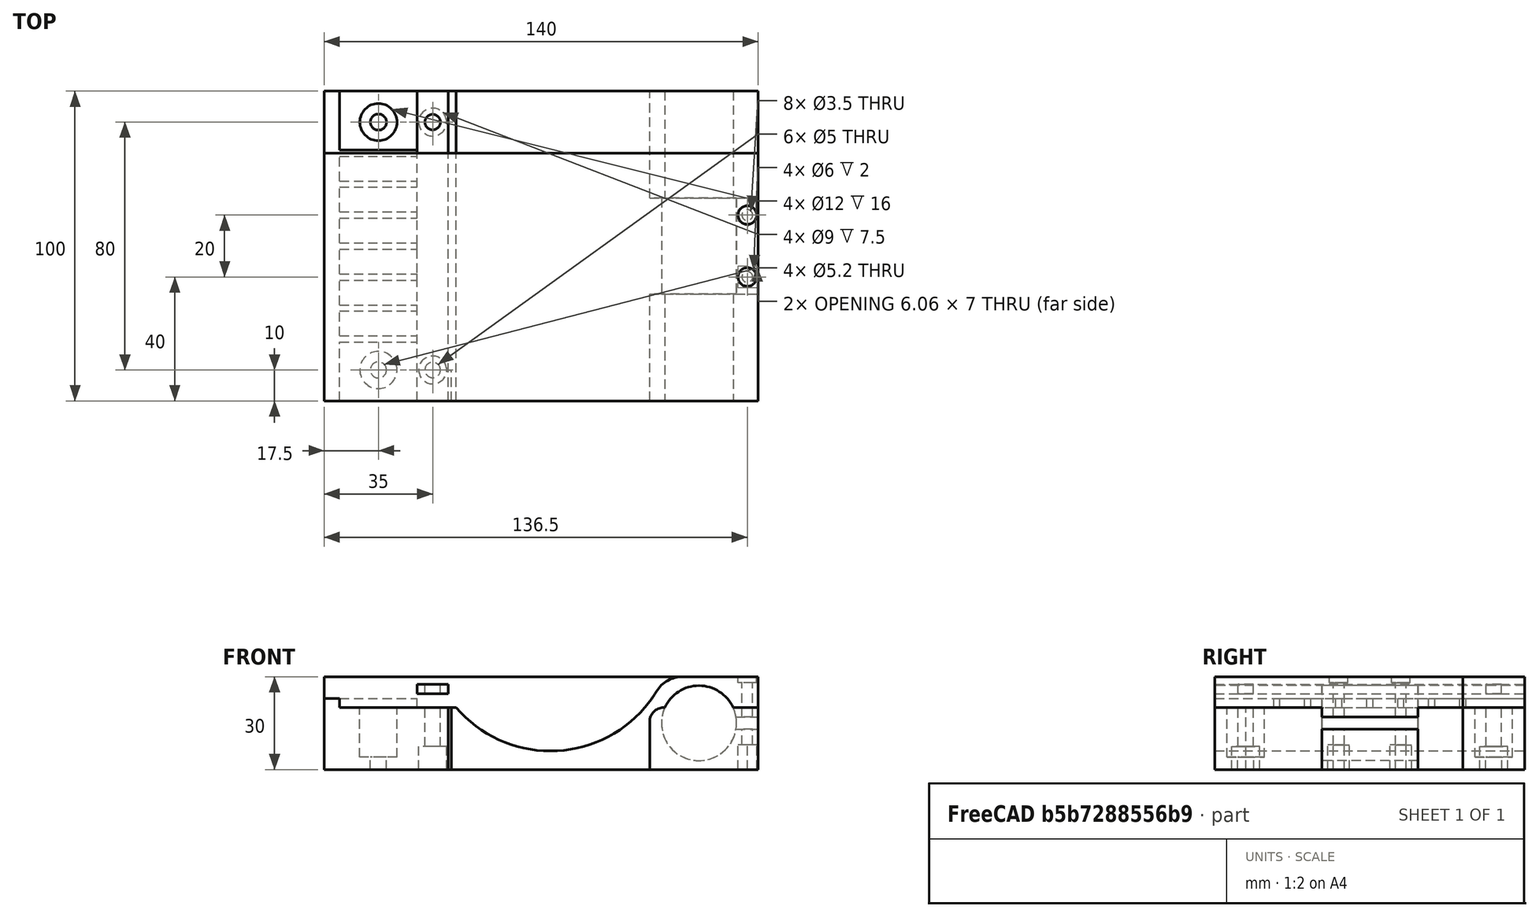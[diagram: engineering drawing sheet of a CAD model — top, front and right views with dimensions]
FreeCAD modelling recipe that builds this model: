
FCSTD DOCUMENT  (FreeCAD 0.18.4R)
Label: vibrator
License: All rights reserved
LicenseURL: http://en.wikipedia.org/wiki/All_rights_reserved
objects: Part::Cylinder×17, Part::Box×16, Part::Cut×10, Part::MultiFuse×5, Part::Fuse×2, Part::RegularPolygon×2, Part::Extrusion×2, PartDesign::Fillet×2, PartDesign::FeatureBase×1, PartDesign::Body×1, Part::Feature×1
note: 59 computed .brp shape members not serialized (recipe doc carries the construction recipe); baked Part::Feature solids carry a one-line shape summary decoded from their .brp

FEATURE [Part::Box] Box  label="Cube"
  AttacherType = Attacher::AttachEngine3D
  Height = 20
  Length = 140
  Width = 100
FEATURE [Part::Cylinder] Cylinder
  Angle = 360
  AttacherType = Attacher::AttachEngine3D
  Height = 20
  Placement = pos=(17.5,10,0) rot=(0,0,1;0rad)
  Radius = 2.6
FEATURE [Part::Cylinder] Cylinder001
  Angle = 360
  AttacherType = Attacher::AttachEngine3D
  Height = 20
  Placement = pos=(17.5,90,0) rot=(0,0,1;0rad)
  Radius = 2.6
FEATURE [Part::Cylinder] Cylinder002
  Angle = 360
  AttacherType = Attacher::AttachEngine3D
  Height = 16
  Placement = pos=(17.5,10,4) rot=(0,0,1;0rad)
  Radius = 6
FEATURE [Part::Cylinder] Cylinder003
  Angle = 360
  AttacherType = Attacher::AttachEngine3D
  Height = 16
  Placement = pos=(17.5,90,4) rot=(0,0,1;0rad)
  Radius = 6
FEATURE [Part::MultiFuse] Fusion
  Shapes = -> [Cylinder,Cylinder002,Cylinder001,Cylinder003]
FEATURE [Part::Cut] Cut
  Base = -> Box
  Tool = -> Fusion
FEATURE [Part::Box] Box001  label="Cube001"
  AttacherType = Attacher::AttachEngine3D
  Height = 3
  Length = 5
  Placement = pos=(0,0,20) rot=(0,0,1;0rad)
  Width = 100
FEATURE [Part::Box] Box002  label="Cube002"
  AttacherType = Attacher::AttachEngine3D
  Height = 3
  Length = 10
  Placement = pos=(30,0,24.5) rot=(0,0,1;0rad)
  Width = 100
FEATURE [Part::Fuse] Fusion001
  Base = -> Cut
  Tool = -> Box001
FEATURE [Part::Box] Box004  label="Cube_far_support"
  AttacherType = Attacher::AttachEngine3D
  Height = 10
  Length = 40
  Placement = pos=(100,0,20) rot=(0,0,1;0rad)
  Width = 100
FEATURE [Part::Box] Box005  label="Cube_delete"
  AttacherType = Attacher::AttachEngine3D
  Height = 30
  Length = 140
  Width = 80
FEATURE [Part::Cylinder] Cylinder004  label="Cylinder_motor"
  Angle = 360
  AttacherType = Attacher::AttachEngine3D
  Height = 31
  Placement = pos=(120.9,65.5,15) rot=(1,0,0;1.5708rad)
  Radius = 12.1
FEATURE [Part::Box] Box006  label="Cube006"
  AttacherType = Attacher::AttachEngine3D
  Height = 3
  Length = 25
  Placement = pos=(5,19,20) rot=(0,0,1;0rad)
  Width = 2
FEATURE [Part::Box] Box007  label="Cube007"
  AttacherType = Attacher::AttachEngine3D
  Height = 3
  Length = 25
  Placement = pos=(5,29,20) rot=(0,0,1;0rad)
  Width = 2
FEATURE [Part::Box] Box008  label="Cube008"
  AttacherType = Attacher::AttachEngine3D
  Height = 3
  Length = 25
  Placement = pos=(5,39,20) rot=(0,0,1;0rad)
  Width = 2
FEATURE [Part::Box] Box009  label="Cube009"
  AttacherType = Attacher::AttachEngine3D
  Height = 3
  Length = 25
  Placement = pos=(5,49,20) rot=(0,0,1;0rad)
  Width = 2
FEATURE [Part::Box] Box010  label="Cube010"
  AttacherType = Attacher::AttachEngine3D
  Height = 3
  Length = 25
  Placement = pos=(5,59,20) rot=(0,0,1;0rad)
  Width = 2
FEATURE [Part::Box] Box011  label="Cube011"
  AttacherType = Attacher::AttachEngine3D
  Height = 3
  Length = 25
  Placement = pos=(5,69,20) rot=(0,0,1;0rad)
  Width = 2
FEATURE [Part::Box] Box012  label="Cube012"
  AttacherType = Attacher::AttachEngine3D
  Height = 3
  Length = 25
  Placement = pos=(5,79,20) rot=(0,0,1;0rad)
  Width = 2
FEATURE [Part::MultiFuse] Fusion004  label="Fusion_tracks"
  Shapes = -> [Box006,Box009,Box008,Box007,Box011,Box010,Box012]
FEATURE [Part::Cylinder] Cylinder005
  Angle = 360
  AttacherType = Attacher::AttachEngine3D
  Height = 20
  Placement = pos=(35,90,0) rot=(0,0,1;0rad)
  Radius = 2.5
FEATURE [Part::Cylinder] Cylinder006
  Angle = 360
  AttacherType = Attacher::AttachEngine3D
  Height = 20
  Placement = pos=(35,10,0) rot=(0,0,1;0rad)
  Radius = 2.5
FEATURE [Part::Cylinder] Cylinder007
  Angle = 360
  AttacherType = Attacher::AttachEngine3D
  Height = 7.5
  Placement = pos=(35,90,0) rot=(0,0,1;0rad)
  Radius = 4.5
FEATURE [Part::Cylinder] Cylinder008
  Angle = 360
  AttacherType = Attacher::AttachEngine3D
  Height = 7.5
  Placement = pos=(35,10,0) rot=(0,0,1;0rad)
  Radius = 4.5
FEATURE [Part::MultiFuse] Fusion005  label="Fusion_1st_support_screw_hole"
  Shapes = -> [Cylinder005,Cylinder008,Cylinder006,Cylinder007]
FEATURE [Part::Cut] Cut002
  Base = -> Fusion001
  Tool = -> Fusion005
FEATURE [Part::Cylinder] Cylinder009
  Angle = 360
  AttacherType = Attacher::AttachEngine3D
  Height = 3
  Placement = pos=(35,10,24.5) rot=(0,0,1;0rad)
  Radius = 2.5
FEATURE [Part::Cylinder] Cylinder010
  Angle = 360
  AttacherType = Attacher::AttachEngine3D
  Height = 3
  Placement = pos=(35,90,24.5) rot=(0,0,1;0rad)
  Radius = 2.5
FEATURE [Part::Cut] Cut003
  Base = -> Box002
  Tool = -> Cylinder009
FEATURE [Part::Cut] Cut004  label="Cut_1st_support_bar"
  Base = -> Cut003
  Tool = -> Cylinder010
FEATURE [Part::Box] Box013  label="Cube013"
  AttacherType = Attacher::AttachEngine3D
  Height = 20
  Length = 35
  Placement = pos=(105,0,0) rot=(0,0,1;0rad)
  Width = 34.5
FEATURE [Part::Box] Box014  label="Cube014"
  AttacherType = Attacher::AttachEngine3D
  Height = 20
  Length = 35
  Placement = pos=(105,65.5,0) rot=(0,0,1;0rad)
  Width = 34.5
FEATURE [Part::Cut] Cut005
  Base = -> Cut002
  Tool = -> Box013
FEATURE [Part::Cut] Cut006
  Base = -> Cut005
  Tool = -> Box014
FEATURE [Part::Cylinder] Cylinder011  label="Cylinder_motor_remove"
  Angle = 360
  AttacherType = Attacher::AttachEngine3D
  Height = 100
  Placement = pos=(120.9,100,15) rot=(1,0,0;1.5708rad)
  Radius = 12.1
FEATURE [Part::Fuse] Fusion006
  Base = -> Cut006
  Tool = -> Box004
FEATURE [Part::Cut] Cut007
  Base = -> Fusion006
  Tool = -> Cylinder011
FEATURE [Part::Cylinder] Cylinder012  label="Cylinder_hole_serrage_01"
  Angle = 360
  AttacherType = Attacher::AttachEngine3D
  Height = 30
  Placement = pos=(136.5,40,0) rot=(0,0,1;0rad)
  Radius = 1.75
FEATURE [Part::Cylinder] Cylinder013  label="Cylinder_hole_serrage_02"
  Angle = 360
  AttacherType = Attacher::AttachEngine3D
  Height = 30
  Placement = pos=(136.5,60,0) rot=(0,0,1;0rad)
  Radius = 1.75
FEATURE [Part::Cylinder] Cylinder014  label="Cylinder_hole_serrage_003"
  Angle = 360
  AttacherType = Attacher::AttachEngine3D
  Height = 2
  Placement = pos=(136.5,40,28) rot=(0,0,1;0rad)
  Radius = 3
FEATURE [Part::Cylinder] Cylinder015  label="Cylinder_hole_serrage_004"
  Angle = 360
  AttacherType = Attacher::AttachEngine3D
  Height = 2
  Placement = pos=(136.5,60,28) rot=(0,0,1;0rad)
  Radius = 3
FEATURE [Part::RegularPolygon] RegularPolygon  label="Regular polygon"
  AttacherType = Attacher::AttachEngine3D
  Circumradius = 3.5
  Polygon = 6
FEATURE [Part::Extrusion] Extrude
  Base = -> RegularPolygon
  Dir = (0,0,1)
  DirMode = 2
  FaceMakerClass = Part::FaceMakerBullseye
  LengthFwd = 8
  LengthRev = 0
  Placement = pos=(136.5,40,0) rot=(0,0,1;0.523599rad)
  Solid = true
  Symmetric = false
FEATURE [Part::RegularPolygon] RegularPolygon001  label="Regular polygon001"
  AttacherType = Attacher::AttachEngine3D
  Circumradius = 3.5
  Polygon = 6
FEATURE [Part::Extrusion] Extrude001
  Base = -> RegularPolygon001
  Dir = (0,0,1)
  DirMode = 2
  FaceMakerClass = Part::FaceMakerBullseye
  LengthFwd = 8
  LengthRev = 0
  Placement = pos=(136.5,60,0) rot=(0,0,1;0.523599rad)
  Solid = true
  Symmetric = false
FEATURE [Part::MultiFuse] Fusion007  label="Fusion_hole_serrage"
  Shapes = -> [Extrude,Cylinder012,Cylinder013,Cylinder015,Cylinder014,Extrude001]
FEATURE [Part::Cut] Cut008
  Base = -> Cut007
  Tool = -> Fusion007
FEATURE [Part::Box] Box015  label="Cube_entrefer"
  AttacherType = Attacher::AttachEngine3D
  Height = 4
  Length = 10
  Placement = pos=(130,0,13) rot=(0,0,1;0rad)
  Width = 100
FEATURE [Part::Cut] Cut009
  Base = -> Cut008
  Tool = -> Box015
FEATURE [Part::Box] Box016  label="Cube015"
  AttacherType = Attacher::AttachEngine3D
  Height = 20
  Length = 1
  Placement = pos=(40,0,0) rot=(0,0,1;0rad)
  Width = 10
FEATURE [Part::Cylinder] Cylinder016  label="Cylinder011"
  Angle = 360
  AttacherType = Attacher::AttachEngine3D
  Height = 100
  Placement = pos=(73,1.02e-14,46) rot=(1,0,0;-1.5708rad)
  Radius = 40
FEATURE [Part::Cut] Cut010
  Base = -> Cut009
  Tool = -> Cylinder016
FEATURE [Part::MultiFuse] Fusion008
  Shapes = -> [Fusion004,Cut010]
FEATURE [PartDesign::FeatureBase] BaseFeature
  BaseFeature = -> Fusion008
FEATURE [PartDesign::Fillet] Fillet
  Base = -> BaseFeature [Edge34]
  BaseFeature = -> BaseFeature
  Radius = 10
FEATURE [PartDesign::Fillet] Fillet001
  Base = -> Fillet [Edge42,Edge129]
  BaseFeature = -> Fillet
  Radius = 4.5
FEATURE [PartDesign::Body] Body
  BaseFeature = -> Fusion008
  Group = -> [BaseFeature,Fillet,Fillet001]
  Origin = -> Origin
  Tip = -> Fillet001
FEATURE [Part::Feature] Fillet001001  label="REFINED"
  shape: bbox 140 x 100 x 30 mm, 89 faces (baked)
